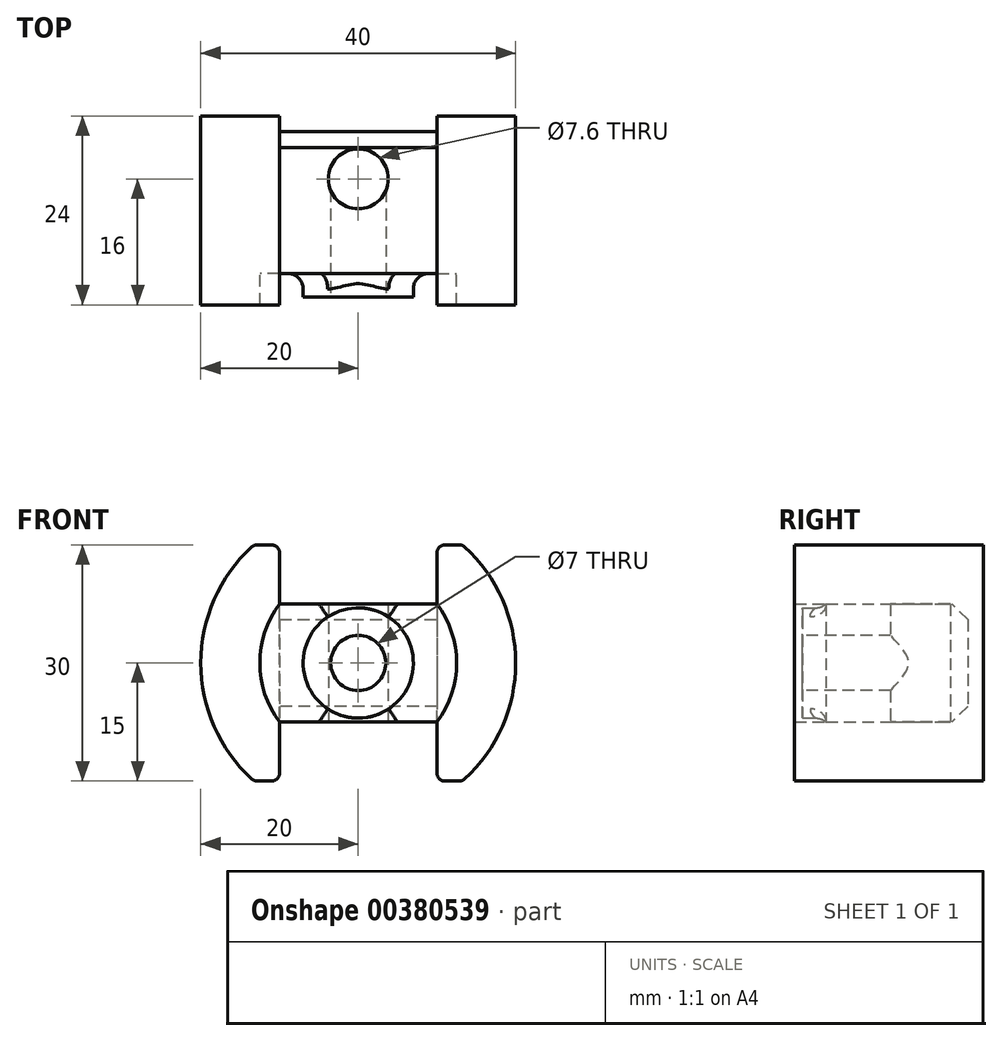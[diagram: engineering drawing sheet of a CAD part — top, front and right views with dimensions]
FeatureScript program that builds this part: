
annotation { "Feature Type Name" : "Feature", "Feature Type Description" : "" }
export const myFeature = defineFeature(function(context is Context, id is Id, definition is map)
    precondition{}
    {
        {
            var Q0;
            Q0=qCreatedBy(makeId("Front.planeOp"),FACE);
            var sketch = newSketch(context, id + "F0", { "sketchPlane" : qUnion([Q0])});
            skArc(sketch, "E0", {"start": v(-13.23, 15) * mm, "mid": v(-20, 0) * mm, "end": v(-13.23, -15) * mm});
            skArc(sketch, "E1", {"start": v(-10, 7.5) * mm, "mid": v(-12.5, 0) * mm, "end": v(-10, -7.5) * mm});
            skLineSegment(sketch, "E2.bottom", {"start": v(-13.23, 15) * mm, "end": v(-10, 15) * mm});
            skLineSegment(sketch, "E2.top", {"start": v(-13.23, -15) * mm, "end": v(-10, -15) * mm});
            skArc(sketch, "E3.trimOffspring", {"start": v(13.23, -15) * mm, "mid": v(20, 0) * mm, "end": v(13.23, 15) * mm});
            skLineSegment(sketch, "E4.bottom", {"start": v(10, 7.5) * mm, "end": v(-10, 7.5) * mm});
            skLineSegment(sketch, "E4.top", {"start": v(10, -7.5) * mm, "end": v(-10, -7.5) * mm});
            skLineSegment(sketch, "E4.left", {"start": v(10, 7.5) * mm, "end": v(10, -7.5) * mm});
            skLineSegment(sketch, "E4.right", {"start": v(-10, 7.5) * mm, "end": v(-10, -7.5) * mm});
            skLineSegment(sketch, "E5", {"start": v(-10, 7.5) * mm, "end": v(-10, 15) * mm});
            skLineSegment(sketch, "E6", {"start": v(10, 7.5) * mm, "end": v(10, 15) * mm});
            skLineSegment(sketch, "E7", {"start": v(10, -7.5) * mm, "end": v(10, -15) * mm});
            skLineSegment(sketch, "E8", {"start": v(-10, -7.5) * mm, "end": v(-10, -15) * mm});
            skLineSegment(sketch, "E9.trimOffspring", {"start": v(10, -15) * mm, "end": v(13.23, -15) * mm});
            skLineSegment(sketch, "E10.trimOffspring", {"start": v(10, 15) * mm, "end": v(13.23, 15) * mm});
            skArc(sketch, "E11.trimOffspring", {"start": v(10, -7.5) * mm, "mid": v(12.5, 0) * mm, "end": v(10, 7.5) * mm});
            skCircle(sketch, "E12", {"center": v(0, 0) * mm, "radius": 7 * mm});
            skCircle(sketch, "E13", {"center": v(0, 0) * mm, "radius": 3.5 * mm});
            skSolve(sketch);
        }
        {
            var Q0;
            Q0=makeQuery(id+"F0.imprint","IMPRINT",FACE,{"disambiguationData":[TD([[makeQuery(id+"F0.imprint","IMPRINT",EDGE,{"derivedFrom":sQuery(id+"F0.wireOp",EDGE,"E0")}),1.0]])]});
            var Q1;
            Q1=makeQuery(id+"F0.imprint","IMPRINT",FACE,{"disambiguationData":[TD([[makeQuery(id+"F0.imprint","IMPRINT",EDGE,{"derivedFrom":sQuery(id+"F0.wireOp",EDGE,"E3.trimOffspring")}),1.0]])]});
            extrude(context, id + "F1", {"entities" : qUnion([Q0, Q1]), "depth" : 24 * mm});
        }
        {
            var Q0;
            Q0=makeQuery(id+"F0.imprint","IMPRINT",FACE,{"disambiguationData":[TD([[makeQuery(id+"F0.imprint","IMPRINT",EDGE,{"derivedFrom":sQuery(id+"F0.wireOp",EDGE,"E1")}),1.0]])]});
            var Q1;
            Q1=makeQuery(id+"F0.imprint","IMPRINT",FACE,{"disambiguationData":[TD([[makeQuery(id+"F0.imprint","IMPRINT",EDGE,{"derivedFrom":sQuery(id+"F0.wireOp",EDGE,"E12")}),1.0]])]});
            var Q2;
            Q2=makeQuery(id+"F0.imprint","IMPRINT",FACE,{"disambiguationData":[TD([[makeQuery(id+"F0.imprint","IMPRINT",EDGE,{"derivedFrom":sQuery(id+"F0.wireOp",EDGE,"E4.bottom")}),1.0]])]});
            var Q3;
            Q3=makeQuery(id+"F0.imprint","IMPRINT",FACE,{"disambiguationData":[TD([[makeQuery(id+"F0.imprint","IMPRINT",EDGE,{"derivedFrom":sQuery(id+"F0.wireOp",EDGE,"E4.left")}),1.0]])]});
            extrude(context, id + "F2", {"entities" : qUnion([Q0, Q1, Q2, Q3]), "operationType" : NewBodyOperationType.ADD, "depth" : 20 * mm, "hasSecondDirection" : true, "secondDirectionOppositeDirection" : false, "secondDirectionDepth" : 2 * mm});
        }
        {
            var Q0;
            Q0=makeQuery(id+"F0.imprint","IMPRINT",FACE,{"disambiguationData":[TD([[makeQuery(id+"F0.imprint","IMPRINT",EDGE,{"derivedFrom":sQuery(id+"F0.wireOp",EDGE,"E12")}),1.0]])]});
            var Q1;
            Q1=makeQuery(id+"F0.imprint","IMPRINT",FACE,{"disambiguationData":[TD([[makeQuery(id+"F0.imprint","IMPRINT",EDGE,{"derivedFrom":sQuery(id+"F0.wireOp",EDGE,"E13")}),1.0]])]});
            extrude(context, id + "F3", {"entities" : qUnion([Q0, Q1]), "operationType" : NewBodyOperationType.ADD, "depth" : 23 * mm, "hasSecondDirection" : true, "secondDirectionOppositeDirection" : false, "secondDirectionDepth" : 2 * mm});
        }
        {
            var Q0;
            Q0=makeQuery(id+"F2.opExtrude","SWEPT_FACE",FACE,{"disambiguationData":[OSD([sQuery(id+"F0.wireOp",EDGE,"E4.top")])]});
            var sketch = newSketch(context, id + "F4", { "sketchPlane" : qUnion([Q0])});
            skLineSegment(sketch, "E14", {"start": v(0, 0) * mm, "end": v(0, 8) * mm});
            skCircle(sketch, "E15", {"center": v(0, 8) * mm, "radius": 3.8 * mm});
            skSolve(sketch);
        }
        {
            var Q0;
            Q0=sQuery(id+"F4.wireOp",VERTEX,"E15.center");
            var Q1;
            Q1=makeQuery(id+"F2.opExtrude","SWEPT_BODY",BODY,{"disambiguationData":[OSD([sQuery(id+"F0.wireOp",EDGE,"E1"),sQuery(id+"F0.wireOp",EDGE,"E4.bottom"),sQuery(id+"F0.wireOp",EDGE,"E4.top"),sQuery(id+"F0.wireOp",EDGE,"E11.trimOffspring"),sQuery(id+"F0.wireOp",EDGE,"E13")])]});
            var Q2;
            Q2=makeQuery(id+"F1.opExtrude","SWEPT_BODY",BODY,{"disambiguationData":[OSD([sQuery(id+"F0.wireOp",EDGE,"E0"),sQuery(id+"F0.wireOp",EDGE,"E1"),sQuery(id+"F0.wireOp",EDGE,"E2.bottom"),sQuery(id+"F0.wireOp",EDGE,"E2.top"),sQuery(id+"F0.wireOp",EDGE,"E5"),sQuery(id+"F0.wireOp",EDGE,"E8")])]});
            hole(context, id + "F5", {"style" : HoleStyle.SIMPLE, "endStyle" : HoleEndStyle.BLIND, "holeDiameter" : 7.6 * mm, "holeDepth" : 17 * mm, "tappedDepth" : 12.7 * mm, "tapClearance" : 3, "locations" : qUnion([Q0]), "scope" : qUnion([Q1, Q2])});
        }
        {
            var Q0;
            Q0=makeQuery(id+"F3.opExtrude","CAP_FACE",FACE,{"disambiguationData":[OSD([sQuery(id+"F0.wireOp",EDGE,"E12")])],"isStart":false});
            var sketch = newSketch(context, id + "F6", { "sketchPlane" : qUnion([Q0])});
            skCircle(sketch, "E16", {"center": v(0, 0) * mm, "radius": 3.5 * mm});
            skSolve(sketch);
        }
        {
            var Q0;
            Q0=sQuery(id+"F6.wireOp",VERTEX,"E16.center");
            var Q1;
            Q1=makeQuery(id+"F2.opExtrude","SWEPT_BODY",BODY,{"disambiguationData":[OSD([sQuery(id+"F0.wireOp",EDGE,"E1"),sQuery(id+"F0.wireOp",EDGE,"E4.bottom"),sQuery(id+"F0.wireOp",EDGE,"E4.top"),sQuery(id+"F0.wireOp",EDGE,"E11.trimOffspring"),sQuery(id+"F0.wireOp",EDGE,"E13")])]});
            var Q2;
            Q2=makeQuery(id+"F1.opExtrude","SWEPT_BODY",BODY,{"disambiguationData":[OSD([sQuery(id+"F0.wireOp",EDGE,"E0"),sQuery(id+"F0.wireOp",EDGE,"E1"),sQuery(id+"F0.wireOp",EDGE,"E2.bottom"),sQuery(id+"F0.wireOp",EDGE,"E2.top"),sQuery(id+"F0.wireOp",EDGE,"E5"),sQuery(id+"F0.wireOp",EDGE,"E8")])]});
            hole(context, id + "F7", {"style" : HoleStyle.SIMPLE, "endStyle" : HoleEndStyle.BLIND, "holeDiameter" : 7 * mm, "holeDepth" : 15 * mm, "tappedDepth" : 12.7 * mm, "tapClearance" : 3, "locations" : qUnion([Q0]), "scope" : qUnion([Q1, Q2])});
        }
        {
            var Q0;
            Q0=makeQuery(id+"F1.opExtrude","SWEPT_EDGE",EDGE,{"disambiguationData":[OSD([sQuery(id+"F0.wireOp",EDGE,"E2.bottom"),sQuery(id+"F0.wireOp",EDGE,"E5")])]});
            var Q1;
            Q1=makeQuery(id+"F1.opExtrude","SWEPT_EDGE",EDGE,{"disambiguationData":[OSD([sQuery(id+"F0.wireOp",EDGE,"E0"),sQuery(id+"F0.wireOp",EDGE,"E2.bottom")])]});
            var Q2;
            Q2=makeQuery(id+"F1.opExtrude","SWEPT_EDGE",EDGE,{"disambiguationData":[OSD([sQuery(id+"F0.wireOp",EDGE,"E2.top"),sQuery(id+"F0.wireOp",EDGE,"E8")])]});
            var Q3;
            Q3=makeQuery(id+"F1.opExtrude","SWEPT_EDGE",EDGE,{"disambiguationData":[OSD([sQuery(id+"F0.wireOp",EDGE,"E0"),sQuery(id+"F0.wireOp",EDGE,"E2.top")])]});
            var Q4;
            Q4=makeQuery(id+"F1.opExtrude","SWEPT_EDGE",EDGE,{"disambiguationData":[OSD([sQuery(id+"F0.wireOp",EDGE,"E3.trimOffspring"),sQuery(id+"F0.wireOp",EDGE,"E10.trimOffspring")])]});
            var Q5;
            Q5=makeQuery(id+"F1.opExtrude","SWEPT_EDGE",EDGE,{"disambiguationData":[OSD([sQuery(id+"F0.wireOp",EDGE,"E6"),sQuery(id+"F0.wireOp",EDGE,"E10.trimOffspring")])]});
            var Q6;
            Q6=makeQuery(id+"F1.opExtrude","SWEPT_EDGE",EDGE,{"disambiguationData":[OSD([sQuery(id+"F0.wireOp",EDGE,"E7"),sQuery(id+"F0.wireOp",EDGE,"E9.trimOffspring")])]});
            var Q7;
            Q7=makeQuery(id+"F1.opExtrude","SWEPT_EDGE",EDGE,{"disambiguationData":[OSD([sQuery(id+"F0.wireOp",EDGE,"E3.trimOffspring"),sQuery(id+"F0.wireOp",EDGE,"E9.trimOffspring")])]});
            fillet(context, id + "F8", {"entities" : qUnion([Q0, Q1, Q2, Q3, Q4, Q5, Q6, Q7]), "radius" : 1 * mm, "tangentPropagation" : true, "allowEdgeOverflow" : false});
        }
        {
            var Q0;
            Q0=makeQuery(id+"F0.imprint","IMPRINT",FACE,{"disambiguationData":[TD([[makeQuery(id+"F0.imprint","IMPRINT",EDGE,{"derivedFrom":sQuery(id+"F0.wireOp",EDGE,"E1")}),1.0]])]});
            var Q1;
            Q1=makeQuery(id+"F0.imprint","IMPRINT",FACE,{"disambiguationData":[TD([[makeQuery(id+"F0.imprint","IMPRINT",EDGE,{"derivedFrom":sQuery(id+"F0.wireOp",EDGE,"E4.left")}),1.0]])]});
            extrude(context, id + "F9", {"entities" : qUnion([Q0, Q1]), "operationType" : NewBodyOperationType.ADD, "depth" : 2 * mm});
        }
        {
            var Q0;
            Q0=makeQuery(id+"F2.opExtrude","CAP_EDGE",EDGE,{"disambiguationData":[OSD([sQuery(id+"F0.wireOp",EDGE,"E4.top")])],"isStart":true});
            var Q1;
            Q1=makeQuery(id+"F2.opExtrude","CAP_EDGE",EDGE,{"disambiguationData":[OSD([sQuery(id+"F0.wireOp",EDGE,"E4.bottom")])],"isStart":true});
            chamfer(context, id + "F10", {"entities" : qUnion([Q0, Q1]), "width" : 2 * mm, "tangentPropagation" : true});
        }
        {
            var Q0;
            Q0=makeQuery(id+"F3.boolean.opBoolean","INTERSECT",EDGE,{"derivedFrom":[makeQuery(id+"F2.opExtrude","CAP_FACE",FACE,{"disambiguationData":[OSD([sQuery(id+"F0.wireOp",EDGE,"E1"),sQuery(id+"F0.wireOp",EDGE,"E4.bottom"),sQuery(id+"F0.wireOp",EDGE,"E4.top"),sQuery(id+"F0.wireOp",EDGE,"E11.trimOffspring"),sQuery(id+"F0.wireOp",EDGE,"E13")])],"isStart":false}),makeQuery(id+"F3.opExtrude","SWEPT_FACE",FACE,{"disambiguationData":[OSD([sQuery(id+"F0.wireOp",EDGE,"E12")])]})]});
            fillet(context, id + "F11", {"entities" : qUnion([Q0]), "radius" : 2 * mm, "tangentPropagation" : true, "allowEdgeOverflow" : false});
        }
    });
